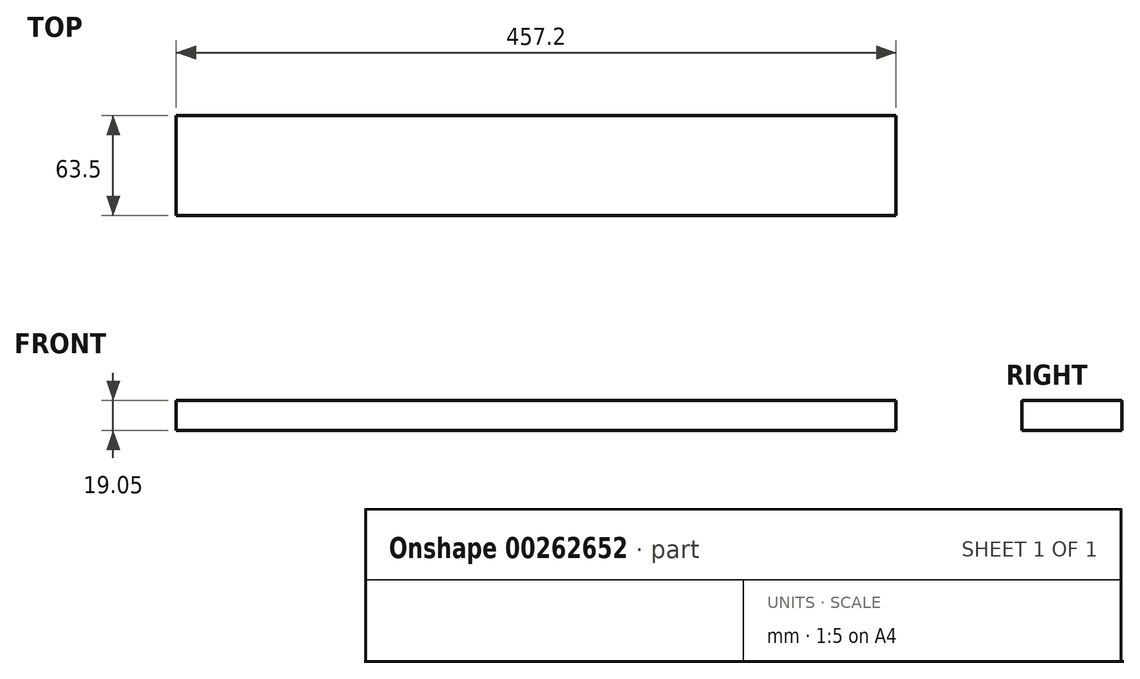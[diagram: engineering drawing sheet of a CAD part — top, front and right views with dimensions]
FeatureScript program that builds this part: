
annotation { "Feature Type Name" : "Feature", "Feature Type Description" : "" }
export const myFeature = defineFeature(function(context is Context, id is Id, definition is map)
    precondition{}
    {
        {
            var Q0;
            Q0=qCreatedBy(makeId("Top.planeOp"),FACE);
            var sketch = newSketch(context, id + "F0", { "sketchPlane" : qUnion([Q0])});
            skLineSegment(sketch, "E0.bottom", {"start": v(0, 0) * mm, "end": v(457.2, 0) * mm});
            skLineSegment(sketch, "E0.top", {"start": v(0, 63.5) * mm, "end": v(457.2, 63.5) * mm});
            skLineSegment(sketch, "E0.left", {"start": v(0, 0) * mm, "end": v(0, 63.5) * mm});
            skLineSegment(sketch, "E0.right", {"start": v(457.2, 0) * mm, "end": v(457.2, 63.5) * mm});
            skSolve(sketch);
        }
        {
            var Q0;
            Q0=makeQuery(id+"F0.imprint","IMPRINT",FACE,{"disambiguationData":[TD([[makeQuery(id+"F0.imprint","IMPRINT",EDGE,{"derivedFrom":sQuery(id+"F0.wireOp",EDGE,"E0.bottom")}),1.0]])]});
            extrude(context, id + "F1", {"entities" : qUnion([Q0]), "depth" : 19.05 * mm, "offsetDistance" : 25.4 * mm});
        }
    });
